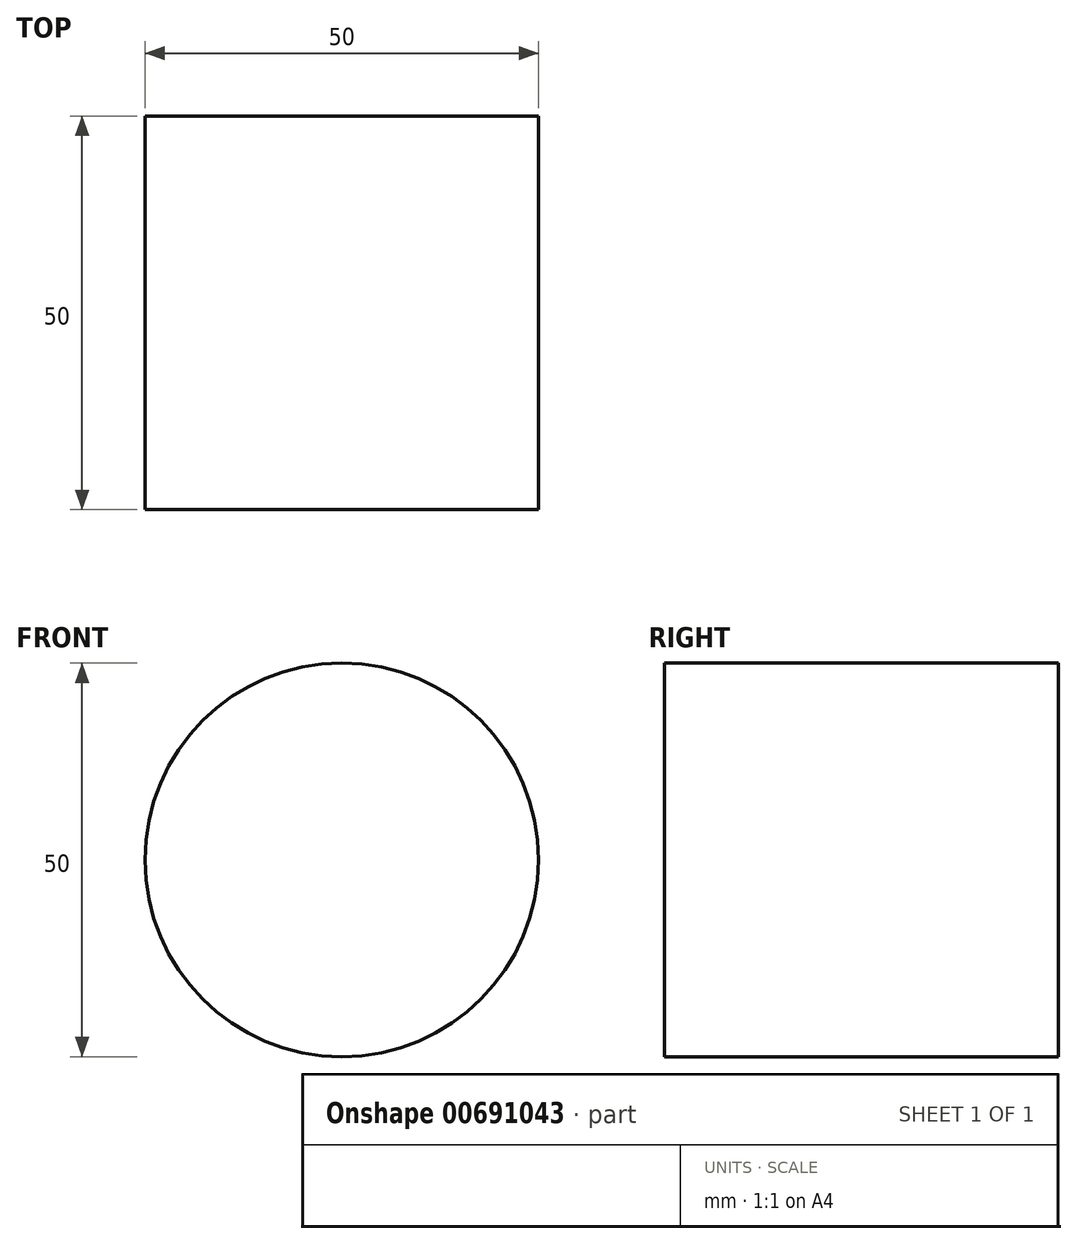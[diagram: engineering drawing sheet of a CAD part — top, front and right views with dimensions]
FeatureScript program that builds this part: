
annotation { "Feature Type Name" : "Feature", "Feature Type Description" : "" }
export const myFeature = defineFeature(function(context is Context, id is Id, definition is map)
    precondition{}
    {
        {
            var Q0;
            Q0=qCreatedBy(makeId("Front.planeOp"),FACE);
            var sketch = newSketch(context, id + "F0", { "sketchPlane" : qUnion([Q0])});
            skCircle(sketch, "E0", {"center": v(0, 0) * mm, "radius": 25 * mm});
            skSolve(sketch);
        }
        {
            var Q0;
            Q0=makeQuery(id+"F0.imprint","IMPRINT",FACE,{"disambiguationData":[TD([[makeQuery(id+"F0.imprint","IMPRINT",EDGE,{"derivedFrom":sQuery(id+"F0.wireOp",EDGE,"E0")}),1.0]])]});
            extrude(context, id + "F1", {"entities" : qUnion([Q0]), "depth" : 50 * mm, "offsetDistance" : 25 * mm});
        }
        {
            var Q0;
            Q0=makeQuery(id+"F1.opExtrude","CAP_FACE",FACE,{"disambiguationData":[OSD([sQuery(id+"F0.wireOp",EDGE,"E0")])],"isStart":false});
            var sketch = newSketch(context, id + "F2", { "sketchPlane" : qUnion([Q0])});
            skCircle(sketch, "E1", {"center": v(0, 0) * mm, "radius": 25 * mm});
            skSolve(sketch);
        }
        {
            var Q0;
            Q0=qCreatedBy(makeId("Front.planeOp"),FACE);
            cPlane(context, id + "F3", {"entities" : qUnion([Q0]), "cplaneType" : CPlaneType.OFFSET, "offset" : 50 * mm, "width" : 150 * mm, "height" : 150 * mm});
        }
    });
